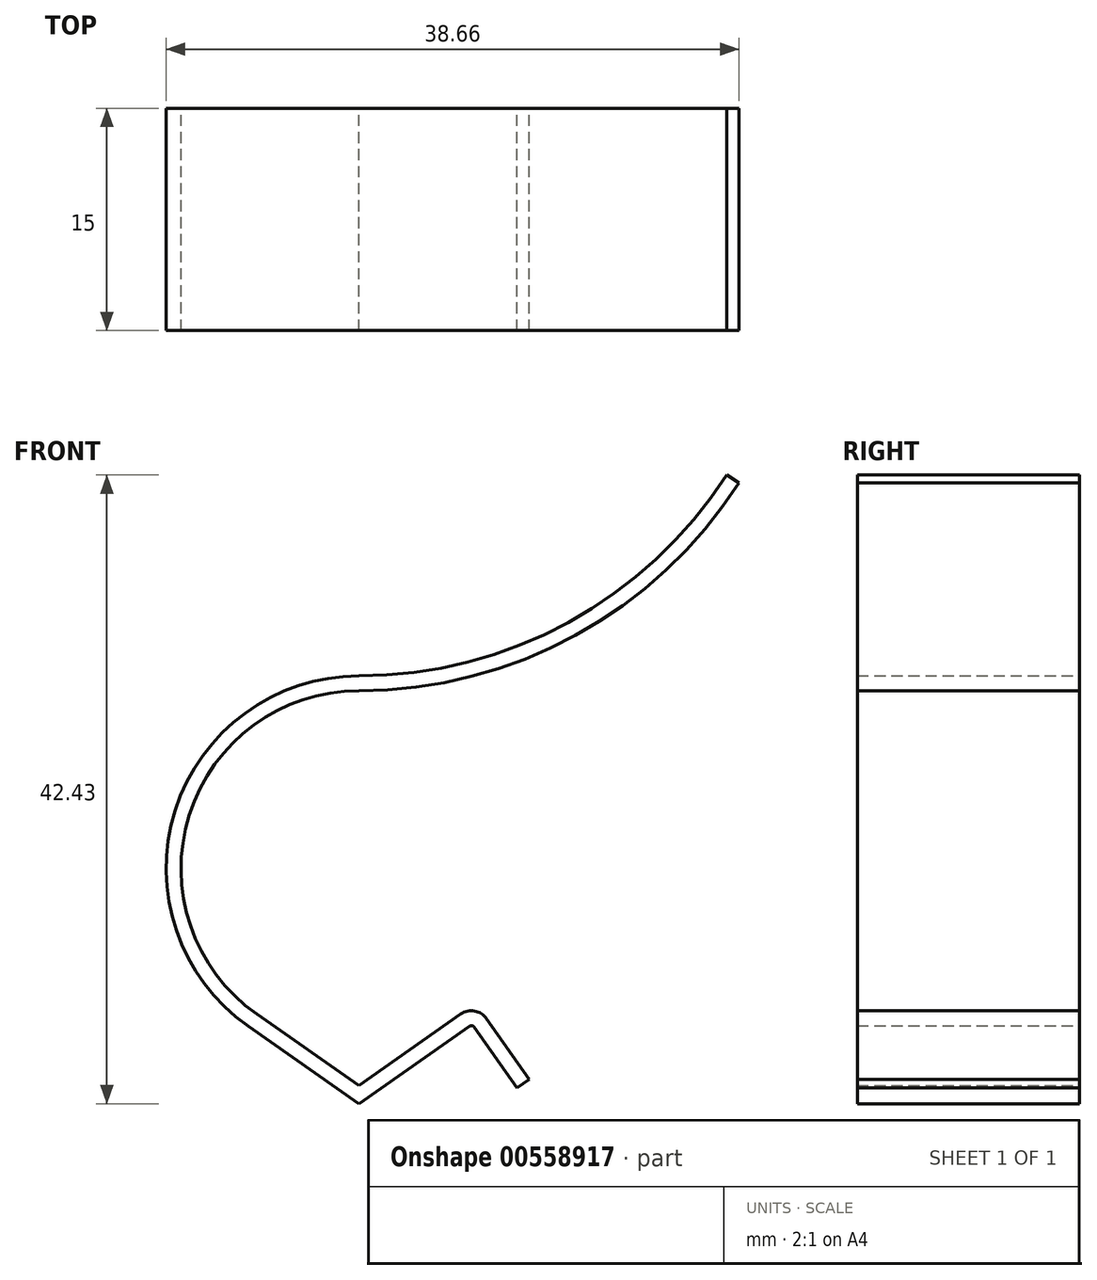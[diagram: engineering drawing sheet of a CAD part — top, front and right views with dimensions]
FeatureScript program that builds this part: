
annotation { "Feature Type Name" : "Feature", "Feature Type Description" : "" }
export const myFeature = defineFeature(function(context is Context, id is Id, definition is map)
    precondition{}
    {
        {
            var Q0;
            Q0=qCreatedBy(makeId("Front.planeOp"),FACE);
            var sketch = newSketch(context, id + "F0", { "sketchPlane" : qUnion([Q0])});
            skArc(sketch, "E0", {"start": v(0, 12.5) * mm, "mid": v(-11.92, 3.76) * mm, "end": v(-7.17, -10.24) * mm});
            skArc(sketch, "E1", {"start": v(0, 12.5) * mm, "mid": v(14.38, 16.17) * mm, "end": v(25.24, 26.3) * mm});
            skLineSegment(sketch, "E2", {"start": v(-7.17, -10.24) * mm, "end": v(0, -15.26) * mm});
            skLineSegment(sketch, "E3", {"start": v(0, -15.26) * mm, "end": v(7.17, -10.24) * mm});
            skLineSegment(sketch, "E4", {"start": v(8.21, -10.42) * mm, "end": v(11.08, -14.52) * mm});
            skPoint(sketch, "E5", {"position": v(25.24, 26.3) * mm});
            skArc(sketch, "E6", {"start": v(8.21, -10.42) * mm, "mid": v(7.73, -10.12) * mm, "end": v(7.17, -10.24) * mm});
            skArc(sketch, "E7.0", {"start": v(0, 13) * mm, "mid": v(14.14, 16.61) * mm, "end": v(24.82, 26.56) * mm});
            skArc(sketch, "E7.1", {"start": v(0, 13) * mm, "mid": v(-12.4, 3.9) * mm, "end": v(-7.46, -10.65) * mm});
            skLineSegment(sketch, "E7.2", {"start": v(7.8, -10.71) * mm, "end": v(10.67, -14.8) * mm});
            skArc(sketch, "E7.3", {"start": v(7.8, -10.71) * mm, "mid": v(7.64, -10.6) * mm, "end": v(7.46, -10.65) * mm});
            skLineSegment(sketch, "E7.4", {"start": v(0, -15.87) * mm, "end": v(7.46, -10.65) * mm});
            skLineSegment(sketch, "E7.5", {"start": v(-7.46, -10.65) * mm, "end": v(0, -15.87) * mm});
            skArc(sketch, "E8.0", {"start": v(0, 12) * mm, "mid": v(14.62, 15.73) * mm, "end": v(25.66, 26.02) * mm});
            skArc(sketch, "E8.1", {"start": v(0, 12) * mm, "mid": v(-11.44, 3.6) * mm, "end": v(-6.88, -9.83) * mm});
            skLineSegment(sketch, "E8.2", {"start": v(8.62, -10.14) * mm, "end": v(11.5, -14.23) * mm});
            skArc(sketch, "E8.3", {"start": v(8.62, -10.14) * mm, "mid": v(7.82, -9.62) * mm, "end": v(6.88, -9.83) * mm});
            skLineSegment(sketch, "E8.4", {"start": v(0, -14.65) * mm, "end": v(6.88, -9.83) * mm});
            skLineSegment(sketch, "E8.5", {"start": v(-6.88, -9.83) * mm, "end": v(0, -14.65) * mm});
            skLineSegment(sketch, "E9", {"start": v(10.67, -14.8) * mm, "end": v(11.5, -14.23) * mm});
            skLineSegment(sketch, "E10", {"start": v(25.66, 26.02) * mm, "end": v(24.82, 26.56) * mm});
            skSolve(sketch);
        }
        {
            var Q0;
            Q0=makeQuery(id+"F0.imprint","IMPRINT",FACE,{"disambiguationData":[TD([[makeQuery(id+"F0.imprint","IMPRINT",EDGE,{"derivedFrom":sQuery(id+"F0.wireOp",EDGE,"E0")}),1.0]])]});
            var Q1;
            Q1=makeQuery(id+"F0.imprint","IMPRINT",FACE,{"disambiguationData":[TD([[makeQuery(id+"F0.imprint","IMPRINT",EDGE,{"derivedFrom":sQuery(id+"F0.wireOp",EDGE,"E0")}),-1.0]])]});
            extrude(context, id + "F1", {"entities" : qUnion([Q0, Q1]), "depth" : 15 * mm, "offsetDistance" : 25 * mm});
        }
    });
